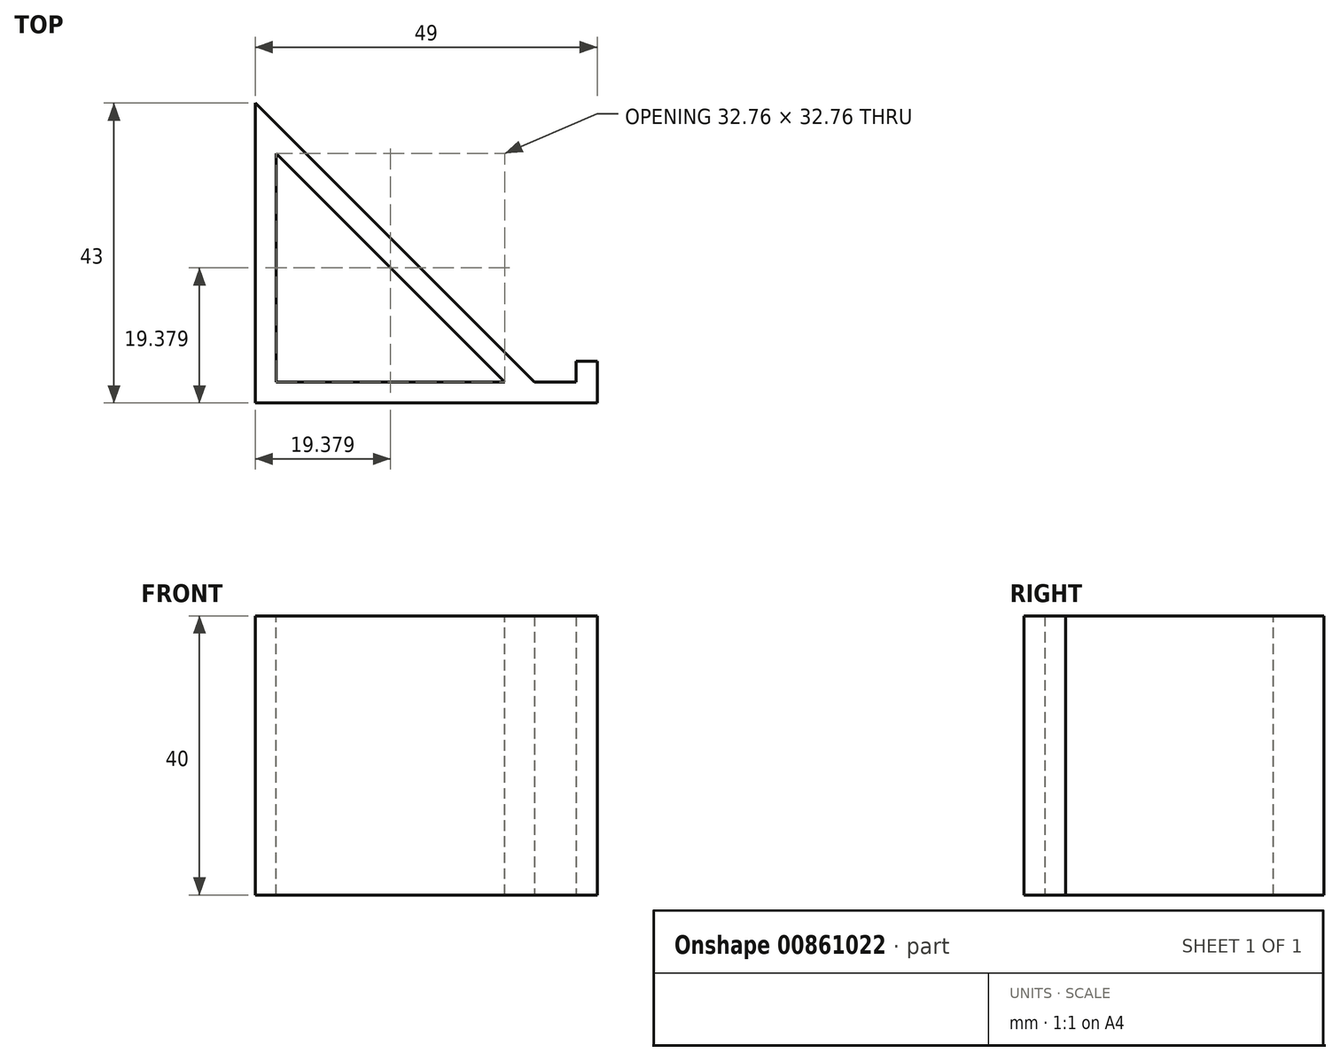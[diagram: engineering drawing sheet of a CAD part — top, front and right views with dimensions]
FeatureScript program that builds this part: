
annotation { "Feature Type Name" : "Feature", "Feature Type Description" : "" }
export const myFeature = defineFeature(function(context is Context, id is Id, definition is map)
    precondition{}
    {
        {
            var Q0;
            Q0=qCreatedBy(makeId("Top.planeOp"),FACE);
            var sketch = newSketch(context, id + "F0", { "sketchPlane" : qUnion([Q0])});
            skLineSegment(sketch, "E0.bottom", {"start": v(0, 0) * mm, "end": v(-40, 0) * mm});
            skLineSegment(sketch, "E0.top", {"start": v(0, 3) * mm, "end": v(-40, 3) * mm});
            skLineSegment(sketch, "E0.left", {"start": v(0, 0) * mm, "end": v(0, 3) * mm});
            skLineSegment(sketch, "E0.right", {"start": v(-40, 0) * mm, "end": v(-40, 3) * mm});
            skPoint(sketch, "E1", {"position": v(-40, 43) * mm});
            skLineSegment(sketch, "E2", {"start": v(-40, 43) * mm, "end": v(0, 3) * mm});
            skPoint(sketch, "E3", {"position": v(0, 0) * mm});
            skPoint(sketch, "E4", {"position": v(9, 0) * mm});
            skLineSegment(sketch, "E5.bottom", {"start": v(0, 0) * mm, "end": v(9, 0) * mm});
            skLineSegment(sketch, "E5.top", {"start": v(0, 3) * mm, "end": v(9, 3) * mm});
            skLineSegment(sketch, "E5.right", {"start": v(9, 0) * mm, "end": v(9, 3) * mm});
            skPoint(sketch, "E6", {"position": v(9, 6) * mm});
            skPoint(sketch, "E7", {"position": v(6, 6) * mm});
            skPoint(sketch, "E8", {"position": v(6, 3) * mm});
            skLineSegment(sketch, "E9", {"start": v(9, 3) * mm, "end": v(9, 6) * mm});
            skLineSegment(sketch, "E10", {"start": v(6, 6) * mm, "end": v(6, 3) * mm});
            skLineSegment(sketch, "E11", {"start": v(9, 6) * mm, "end": v(6, 6) * mm});
            skLineSegment(sketch, "E12", {"start": v(-40, 43) * mm, "end": v(-40, 3) * mm});
            skSolve(sketch);
        }
        {
            var Q0;
            Q0 = qSketchRegion(id + "F0", true);
            extrude(context, id + "F1", {"entities" : qUnion([Q0]), "depth" : 40 * mm, "offsetDistance" : 25 * mm});
        }
        {
            var Q0;
            Q0=makeQuery(id+"F1.opExtrude","CAP_FACE",FACE,{"disambiguationData":[OSD([sQuery(id+"F0.wireOp",EDGE,"E0.bottom"),sQuery(id+"F0.wireOp",EDGE,"E0.right"),sQuery(id+"F0.wireOp",EDGE,"E2"),sQuery(id+"F0.wireOp",EDGE,"E5.bottom"),sQuery(id+"F0.wireOp",EDGE,"E5.top"),sQuery(id+"F0.wireOp",EDGE,"E5.right"),sQuery(id+"F0.wireOp",EDGE,"E9"),sQuery(id+"F0.wireOp",EDGE,"E10"),sQuery(id+"F0.wireOp",EDGE,"E11"),sQuery(id+"F0.wireOp",EDGE,"E12")])],"isStart":false});
            var sketch = newSketch(context, id + "F2", { "sketchPlane" : qUnion([Q0])});
            skLineSegment(sketch, "E13", {"start": v(-40, 43) * mm, "end": v(3, 0) * mm});
            skSolve(sketch);
        }
        {
            var Q0;
            {var subQ2=makeQuery(id+"F1.opExtrude","CAP_EDGE",EDGE,{"disambiguationData":[OSD([sQuery(id+"F0.wireOp",EDGE,"E0.right"),sQuery(id+"F0.wireOp",EDGE,"E12")])],"isStart":false});Q0=makeQuery(id+"F2.imprint","IMPRINT",FACE,{"disambiguationData":[TD([[makeQuery(id+"F2.imprint","IMPRINT",EDGE,{"derivedFrom":subQ2}),1.0]])]});}
            var sketch = newSketch(context, id + "F3", { "sketchPlane" : qUnion([Q0])});
            skLineSegment(sketch, "E14", {"start": v(-37, 35.76) * mm, "end": v(-4.24, 3) * mm});
            skLineSegment(sketch, "E15", {"start": v(-4.24, 3) * mm, "end": v(-37, 3) * mm});
            skLineSegment(sketch, "E16", {"start": v(-37, 3) * mm, "end": v(-37, 35.76) * mm});
            skSolve(sketch);
        }
        {
            var Q0;
            Q0 = qSketchRegion(id + "F3", true);
            extrude(context, id + "F4", {"entities" : qUnion([Q0]), "operationType" : NewBodyOperationType.REMOVE, "endBound" : BoundingType.THROUGH_ALL, "oppositeDirection" : true, "depth" : 25 * mm, "offsetDistance" : 25 * mm});
        }
    });
